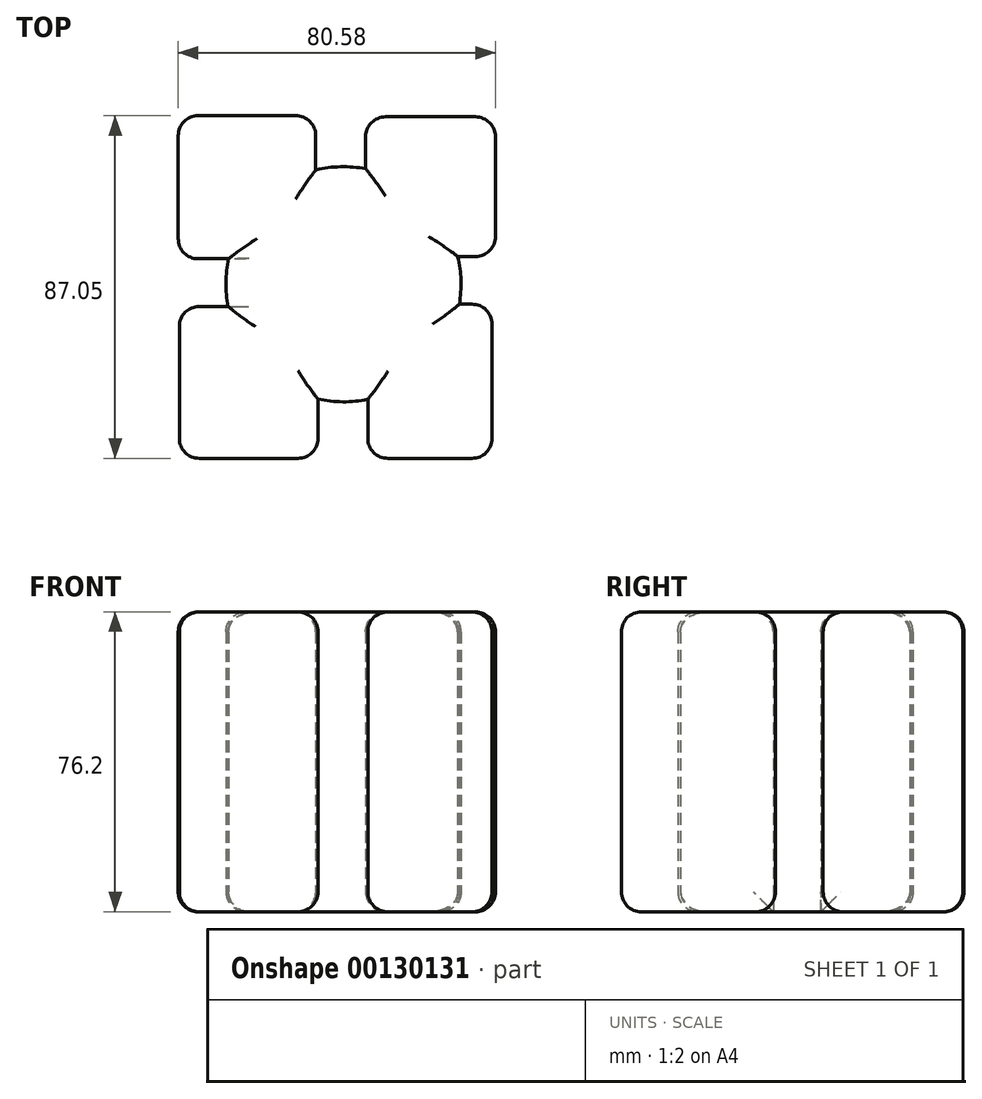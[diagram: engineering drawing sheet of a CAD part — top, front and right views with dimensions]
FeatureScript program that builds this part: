
annotation { "Feature Type Name" : "Feature", "Feature Type Description" : "" }
export const myFeature = defineFeature(function(context is Context, id is Id, definition is map)
    precondition{}
    {
        {
            var Q0;
            Q0=qCreatedBy(makeId("Top.planeOp"),FACE);
            var sketch = newSketch(context, id + "F0", { "sketchPlane" : qUnion([Q0])});
            skArc(sketch, "E0", {"start": v(-29.16, 6.48) * mm, "mid": v(-29.87, 0.43) * mm, "end": v(-29.33, -5.63) * mm});
            skLineSegment(sketch, "E1.bottom", {"start": v(-41.98, 42.82) * mm, "end": v(-7.04, 42.82) * mm});
            skLineSegment(sketch, "E1.top", {"start": v(-41.98, 6.48) * mm, "end": v(-29.16, 6.48) * mm});
            skLineSegment(sketch, "E1.left", {"start": v(-41.98, 42.82) * mm, "end": v(-41.98, 6.48) * mm});
            skLineSegment(sketch, "E1.right", {"start": v(-7.04, 42.82) * mm, "end": v(-7.04, 29.03) * mm});
            skLineSegment(sketch, "E2.bottom", {"start": v(5.63, 42.54) * mm, "end": v(38.6, 42.54) * mm});
            skLineSegment(sketch, "E2.top", {"start": v(29.03, 7.04) * mm, "end": v(38.6, 7.04) * mm});
            skLineSegment(sketch, "E2.left", {"start": v(5.63, 42.54) * mm, "end": v(5.63, 29.33) * mm});
            skLineSegment(sketch, "E2.right", {"start": v(38.6, 42.54) * mm, "end": v(38.6, 7.04) * mm});
            skLineSegment(sketch, "E3.bottom", {"start": v(-41.7, -5.63) * mm, "end": v(-29.33, -5.63) * mm});
            skLineSegment(sketch, "E3.top", {"start": v(-41.7, -44.23) * mm, "end": v(-6.48, -44.23) * mm});
            skLineSegment(sketch, "E3.left", {"start": v(-41.7, -5.63) * mm, "end": v(-41.7, -44.23) * mm});
            skLineSegment(sketch, "E3.right", {"start": v(-6.48, -29.16) * mm, "end": v(-6.48, -44.23) * mm});
            skLineSegment(sketch, "E4.bottom", {"start": v(29.43, -5.07) * mm, "end": v(37.75, -5.07) * mm});
            skLineSegment(sketch, "E4.top", {"start": v(6.2, -44.23) * mm, "end": v(37.75, -44.23) * mm});
            skLineSegment(sketch, "E4.left", {"start": v(6.2, -29.22) * mm, "end": v(6.2, -44.23) * mm});
            skLineSegment(sketch, "E4.right", {"start": v(37.75, -5.07) * mm, "end": v(37.75, -44.23) * mm});
            skArc(sketch, "E5.trimOffspring", {"start": v(-6.48, -29.16) * mm, "mid": v(-0.14, -29.87) * mm, "end": v(6.2, -29.22) * mm});
            skArc(sketch, "E6.trimOffspring", {"start": v(29.43, -5.07) * mm, "mid": v(29.85, 1) * mm, "end": v(29.03, 7.04) * mm});
            skArc(sketch, "E7.trimOffspring", {"start": v(5.63, 29.33) * mm, "mid": v(-0.72, 29.86) * mm, "end": v(-7.04, 29.03) * mm});
            skSolve(sketch);
        }
        {
            var Q0;
            Q0=makeQuery(id+"F0.imprint","IMPRINT",FACE,{"disambiguationData":[TD([[makeQuery(id+"F0.imprint","IMPRINT",EDGE,{"derivedFrom":sQuery(id+"F0.wireOp",EDGE,"E0")}),1.0]])]});
            extrude(context, id + "F1", {"entities" : qUnion([Q0]), "depth" : 76.2 * mm});
        }
        {
            var Q0;
            Q0=makeQuery(id+"F1.opExtrude","SWEPT_EDGE",EDGE,{"disambiguationData":[OSD([sQuery(id+"F0.wireOp",EDGE,"E2.top"),sQuery(id+"F0.wireOp",EDGE,"E2.right")])]});
            var Q1;
            Q1=makeQuery(id+"F1.opExtrude","SWEPT_EDGE",EDGE,{"disambiguationData":[OSD([sQuery(id+"F0.wireOp",EDGE,"E2.bottom"),sQuery(id+"F0.wireOp",EDGE,"E2.right")])]});
            var Q2;
            Q2=makeQuery(id+"F1.opExtrude","SWEPT_EDGE",EDGE,{"disambiguationData":[OSD([sQuery(id+"F0.wireOp",EDGE,"E4.bottom"),sQuery(id+"F0.wireOp",EDGE,"E4.right")])]});
            var Q3;
            Q3=makeQuery(id+"F1.opExtrude","SWEPT_EDGE",EDGE,{"disambiguationData":[OSD([sQuery(id+"F0.wireOp",EDGE,"E4.top"),sQuery(id+"F0.wireOp",EDGE,"E4.right")])]});
            var Q4;
            Q4=makeQuery(id+"F1.opExtrude","SWEPT_EDGE",EDGE,{"disambiguationData":[OSD([sQuery(id+"F0.wireOp",EDGE,"E4.top"),sQuery(id+"F0.wireOp",EDGE,"E4.left")])]});
            var Q5;
            Q5=makeQuery(id+"F1.opExtrude","SWEPT_EDGE",EDGE,{"disambiguationData":[OSD([sQuery(id+"F0.wireOp",EDGE,"E3.top"),sQuery(id+"F0.wireOp",EDGE,"E3.right")])]});
            var Q6;
            Q6=makeQuery(id+"F1.opExtrude","SWEPT_EDGE",EDGE,{"disambiguationData":[OSD([sQuery(id+"F0.wireOp",EDGE,"E2.bottom"),sQuery(id+"F0.wireOp",EDGE,"E2.left")])]});
            var Q7;
            Q7=makeQuery(id+"F1.opExtrude","SWEPT_EDGE",EDGE,{"disambiguationData":[OSD([sQuery(id+"F0.wireOp",EDGE,"E1.bottom"),sQuery(id+"F0.wireOp",EDGE,"E1.right")])]});
            var Q8;
            Q8=makeQuery(id+"F1.opExtrude","SWEPT_EDGE",EDGE,{"disambiguationData":[OSD([sQuery(id+"F0.wireOp",EDGE,"E1.bottom"),sQuery(id+"F0.wireOp",EDGE,"E1.left")])]});
            var Q9;
            Q9=makeQuery(id+"F1.opExtrude","SWEPT_EDGE",EDGE,{"disambiguationData":[OSD([sQuery(id+"F0.wireOp",EDGE,"E1.top"),sQuery(id+"F0.wireOp",EDGE,"E1.left")])]});
            var Q10;
            Q10=makeQuery(id+"F1.opExtrude","SWEPT_FACE",FACE,{"disambiguationData":[OSD([sQuery(id+"F0.wireOp",EDGE,"E1.left")])]});
            var Q11;
            Q11=makeQuery(id+"F1.opExtrude","SWEPT_FACE",FACE,{"disambiguationData":[OSD([sQuery(id+"F0.wireOp",EDGE,"E3.left")])]});
            fillet(context, id + "F2", {"entities" : qUnion([Q0, Q1, Q2, Q3, Q4, Q5, Q6, Q7, Q8, Q9, Q10, Q11]), "radius" : 5.08 * mm, "tangentPropagation" : true, "allowEdgeOverflow" : false});
        }
        {
            var Q0;
            Q0=makeQuery(id+"F1.opExtrude","CAP_EDGE",EDGE,{"disambiguationData":[OSD([sQuery(id+"F0.wireOp",EDGE,"E2.right")])],"isStart":false});
            var Q1;
            Q1=makeQuery(id+"F1.opExtrude","CAP_EDGE",EDGE,{"disambiguationData":[OSD([sQuery(id+"F0.wireOp",EDGE,"E1.bottom")])],"isStart":false});
            var Q2;
            Q2=makeQuery(id+"F1.opExtrude","CAP_FACE",FACE,{"disambiguationData":[OSD([sQuery(id+"F0.wireOp",EDGE,"E0"),sQuery(id+"F0.wireOp",EDGE,"E1.bottom"),sQuery(id+"F0.wireOp",EDGE,"E1.top"),sQuery(id+"F0.wireOp",EDGE,"E1.left"),sQuery(id+"F0.wireOp",EDGE,"E1.right"),sQuery(id+"F0.wireOp",EDGE,"E2.bottom"),sQuery(id+"F0.wireOp",EDGE,"E2.top"),sQuery(id+"F0.wireOp",EDGE,"E2.left"),sQuery(id+"F0.wireOp",EDGE,"E2.right"),sQuery(id+"F0.wireOp",EDGE,"E3.bottom"),sQuery(id+"F0.wireOp",EDGE,"E3.top"),sQuery(id+"F0.wireOp",EDGE,"E3.left"),sQuery(id+"F0.wireOp",EDGE,"E3.right"),sQuery(id+"F0.wireOp",EDGE,"E4.bottom"),sQuery(id+"F0.wireOp",EDGE,"E4.top"),sQuery(id+"F0.wireOp",EDGE,"E4.left"),sQuery(id+"F0.wireOp",EDGE,"E4.right"),sQuery(id+"F0.wireOp",EDGE,"E5.trimOffspring"),sQuery(id+"F0.wireOp",EDGE,"E6.trimOffspring"),sQuery(id+"F0.wireOp",EDGE,"E7.trimOffspring")])],"isStart":false});
            fillet(context, id + "F3", {"entities" : qUnion([Q0, Q1, Q2]), "radius" : 5.08 * mm, "tangentPropagation" : true, "allowEdgeOverflow" : false});
        }
        {
            var Q0;
            Q0=makeQuery(id+"F1.opExtrude","CAP_EDGE",EDGE,{"disambiguationData":[OSD([sQuery(id+"F0.wireOp",EDGE,"E4.top")])],"isStart":true});
            var Q1;
            Q1=makeQuery(id+"F1.opExtrude","CAP_EDGE",EDGE,{"disambiguationData":[OSD([sQuery(id+"F0.wireOp",EDGE,"E2.top")])],"isStart":true});
            var Q2;
            Q2=makeQuery(id+"F1.opExtrude","CAP_EDGE",EDGE,{"disambiguationData":[OSD([sQuery(id+"F0.wireOp",EDGE,"E6.trimOffspring")])],"isStart":true});
            var Q3;
            Q3=makeQuery(id+"F1.opExtrude","CAP_EDGE",EDGE,{"disambiguationData":[OSD([sQuery(id+"F0.wireOp",EDGE,"E1.bottom")])],"isStart":true});
            var Q4;
            Q4=makeQuery(id+"F1.opExtrude","CAP_EDGE",EDGE,{"disambiguationData":[OSD([sQuery(id+"F0.wireOp",EDGE,"E7.trimOffspring")])],"isStart":true});
            var Q5;
            Q5=makeQuery(id+"F1.opExtrude","CAP_EDGE",EDGE,{"disambiguationData":[OSD([sQuery(id+"F0.wireOp",EDGE,"E0")])],"isStart":true});
            var Q6;
            Q6=makeQuery(id+"F1.opExtrude","CAP_EDGE",EDGE,{"disambiguationData":[OSD([sQuery(id+"F0.wireOp",EDGE,"E3.top")])],"isStart":true});
            var Q7;
            Q7=makeQuery(id+"F1.opExtrude","CAP_EDGE",EDGE,{"disambiguationData":[OSD([sQuery(id+"F0.wireOp",EDGE,"E5.trimOffspring")])],"isStart":true});
            fillet(context, id + "F4", {"entities" : qUnion([Q0, Q1, Q2, Q3, Q4, Q5, Q6, Q7]), "radius" : 5.08 * mm, "tangentPropagation" : true, "allowEdgeOverflow" : false});
        }
    });
